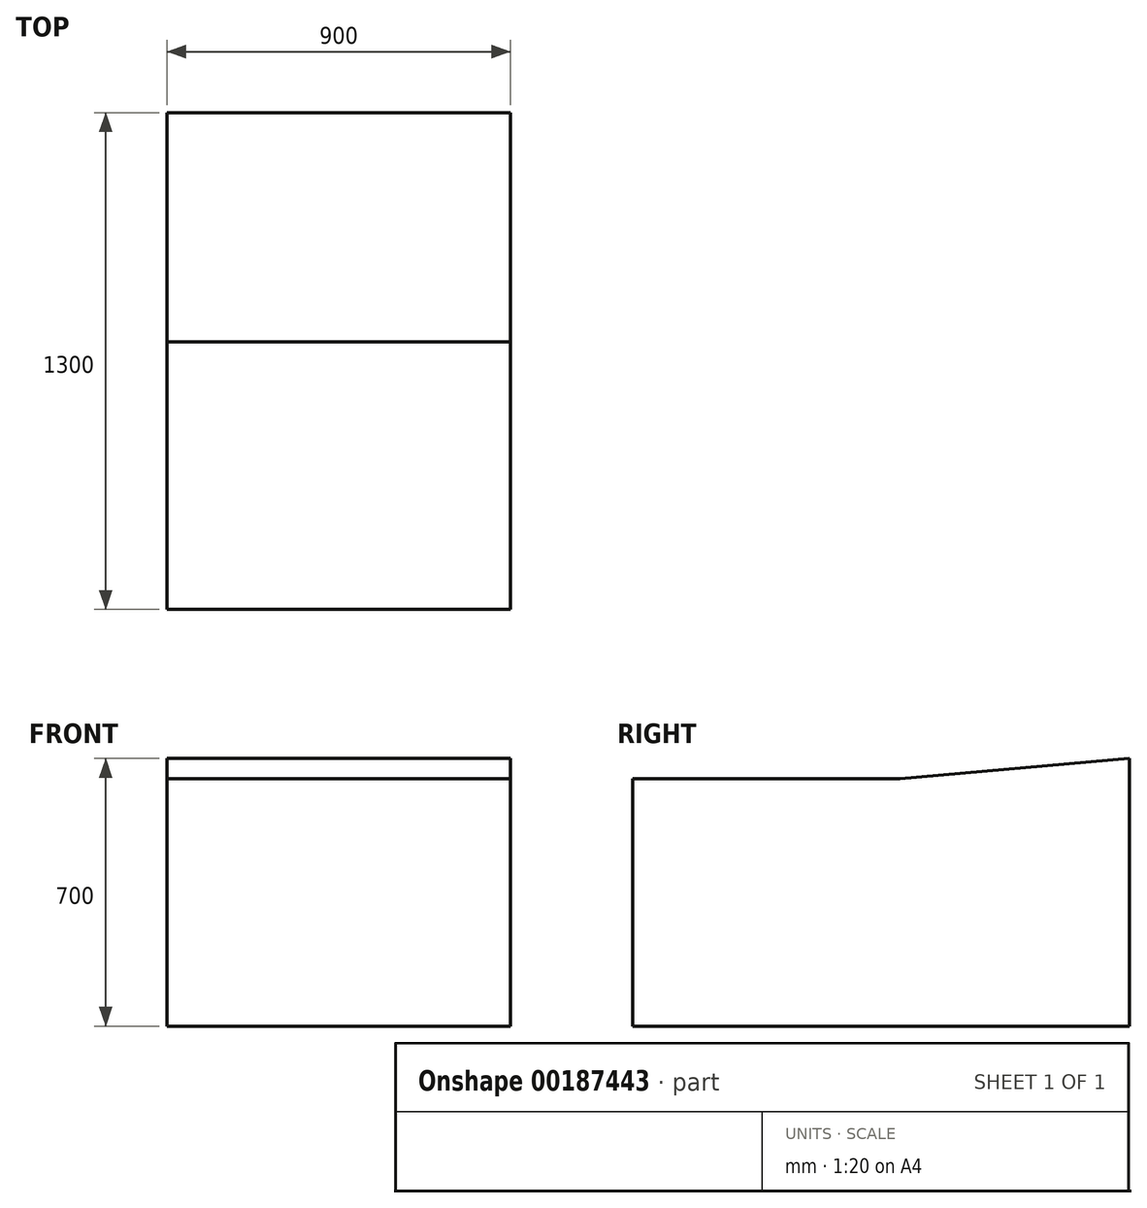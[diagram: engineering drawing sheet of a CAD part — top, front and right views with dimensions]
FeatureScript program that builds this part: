
annotation { "Feature Type Name" : "Feature", "Feature Type Description" : "" }
export const myFeature = defineFeature(function(context is Context, id is Id, definition is map)
    precondition{}
    {
        {
            var Q0;
            Q0=qCreatedBy(makeId("Right.planeOp"),FACE);
            var sketch = newSketch(context, id + "F0", { "sketchPlane" : qUnion([Q0])});
            skLineSegment(sketch, "E0.top", {"start": v(-650, -350) * mm, "end": v(650, -350) * mm});
            skLineSegment(sketch, "E0.left", {"start": v(-650, 297.5) * mm, "end": v(-650, -350) * mm});
            skLineSegment(sketch, "E0.right", {"start": v(650, 350) * mm, "end": v(650, -350) * mm});
            skPoint(sketch, "E0.middle", {"position": v(0, 0) * mm});
            skLineSegment(sketch, "E1", {"start": v(650, 350) * mm, "end": v(50, 297.5) * mm});
            skLineSegment(sketch, "E2", {"start": v(50, 297.5) * mm, "end": v(-650, 297.5) * mm});
            skSolve(sketch);
        }
        {
            var Q0;
            Q0 = qSketchRegion(id + "F0", true);
            extrude(context, id + "F1", {"entities" : qUnion([Q0]), "endBound" : BoundingType.SYMMETRIC, "depth" : 900 * mm, "offsetDistance" : 25 * mm});
        }
    });
